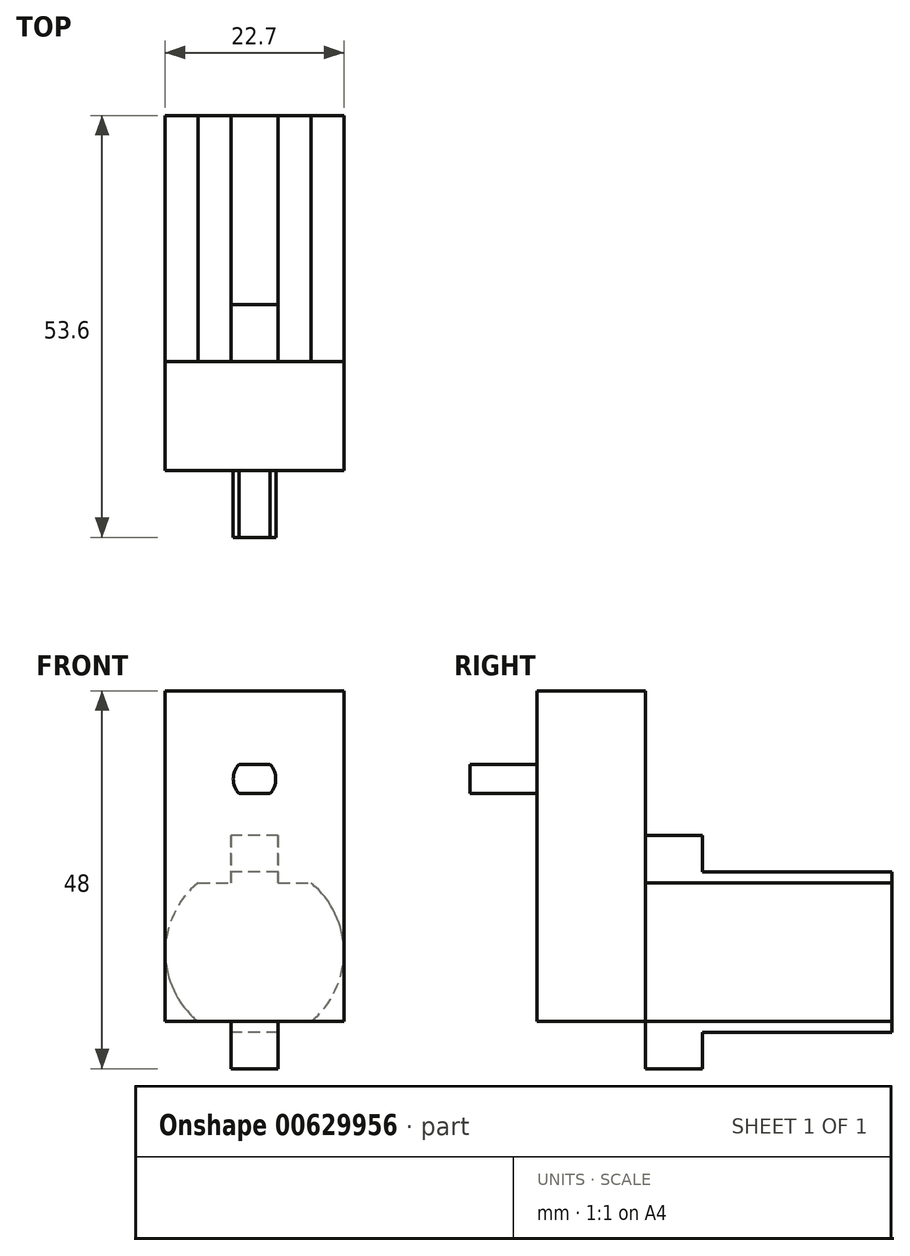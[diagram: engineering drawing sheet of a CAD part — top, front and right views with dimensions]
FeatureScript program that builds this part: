
annotation { "Feature Type Name" : "Feature", "Feature Type Description" : "" }
export const myFeature = defineFeature(function(context is Context, id is Id, definition is map)
    precondition{}
    {
        {
            var Q0;
            Q0=qCreatedBy(makeId("Front.planeOp"),FACE);
            var sketch = newSketch(context, id + "F0", { "sketchPlane" : qUnion([Q0])});
            skLineSegment(sketch, "E0.bottom", {"start": v(-11.35, 11.2) * mm, "end": v(11.35, 11.2) * mm});
            skLineSegment(sketch, "E0.top", {"start": v(-11.35, -30.8) * mm, "end": v(11.35, -30.8) * mm});
            skLineSegment(sketch, "E0.left", {"start": v(-11.35, 11.2) * mm, "end": v(-11.35, -30.8) * mm});
            skLineSegment(sketch, "E0.right", {"start": v(11.35, 11.2) * mm, "end": v(11.35, -30.8) * mm});
            skLineSegment(sketch, "E1", {"start": v(0, 11.2) * mm, "end": v(0, 0) * mm, "construction": true});
            skSolve(sketch);
        }
        {
            var Q0;
            Q0 = qSketchRegion(id + "F0", true);
            extrude(context, id + "F1", {"entities" : qUnion([Q0]), "oppositeDirection" : true, "depth" : 13.8 * mm, "offsetDistance" : 25.4 * mm});
        }
        {
            var Q0;
            Q0=makeQuery(id+"F1.opExtrude","CAP_FACE",FACE,{"disambiguationData":[OSD([sQuery(id+"F0.wireOp",EDGE,"E0.bottom"),sQuery(id+"F0.wireOp",EDGE,"E0.top"),sQuery(id+"F0.wireOp",EDGE,"E0.left"),sQuery(id+"F0.wireOp",EDGE,"E0.right")])],"isStart":true});
            var sketch = newSketch(context, id + "F2", { "sketchPlane" : qUnion([Q0])});
            skArc(sketch, "E2", {"start": v(-1.97, 1.85) * mm, "mid": v(-2.7, 0) * mm, "end": v(-1.97, -1.85) * mm});
            skLineSegment(sketch, "E3", {"start": v(-1.97, 1.85) * mm, "end": v(1.97, 1.85) * mm});
            skLineSegment(sketch, "E4", {"start": v(1.97, -1.85) * mm, "end": v(-1.97, -1.85) * mm});
            skArc(sketch, "E5.trimOffspring", {"start": v(1.97, -1.85) * mm, "mid": v(2.7, 0) * mm, "end": v(1.97, 1.85) * mm});
            skSolve(sketch);
        }
        {
            var Q0;
            Q0 = qSketchRegion(id + "F2", true);
            extrude(context, id + "F3", {"entities" : qUnion([Q0]), "operationType" : NewBodyOperationType.ADD, "depth" : 8.5 * mm, "offsetDistance" : 25.4 * mm});
        }
        {
            var Q0;
            Q0=makeQuery(id+"F1.opExtrude","CAP_FACE",FACE,{"disambiguationData":[OSD([sQuery(id+"F0.wireOp",EDGE,"E0.bottom"),sQuery(id+"F0.wireOp",EDGE,"E0.top"),sQuery(id+"F0.wireOp",EDGE,"E0.left"),sQuery(id+"F0.wireOp",EDGE,"E0.right")])],"isStart":true});
            var sketch = newSketch(context, id + "F4", { "sketchPlane" : qUnion([Q0])});
            skArc(sketch, "E6", {"start": v(-7.17, -13.2) * mm, "mid": v(-11.35, -22) * mm, "end": v(-7.17, -30.8) * mm});
            skLineSegment(sketch, "E7", {"start": v(-7.17, -30.8) * mm, "end": v(7.17, -30.8) * mm});
            skLineSegment(sketch, "E8", {"start": v(-7.17, -13.2) * mm, "end": v(7.17, -13.2) * mm});
            skArc(sketch, "E9.trimOffspring", {"start": v(7.17, -30.8) * mm, "mid": v(11.35, -22) * mm, "end": v(7.17, -13.2) * mm});
            skSolve(sketch);
        }
        {
            var Q0;
            Q0 = qSketchRegion(id + "F4", true);
            extrude(context, id + "F5", {"entities" : qUnion([Q0]), "operationType" : NewBodyOperationType.ADD, "oppositeDirection" : true, "depth" : 45.1 * mm, "offsetDistance" : 25.4 * mm});
        }
        {
            var Q0;
            Q0=qCreatedBy(makeId("Right.planeOp"),FACE);
            var sketch = newSketch(context, id + "F6", { "sketchPlane" : qUnion([Q0])});
            skLineSegment(sketch, "E10", {"start": v(13.8, -7.2) * mm, "end": v(21.07, -7.2) * mm});
            skLineSegment(sketch, "E11", {"start": v(21.07, -7.2) * mm, "end": v(21.07, -11.8) * mm});
            skLineSegment(sketch, "E12", {"start": v(21.07, -11.8) * mm, "end": v(45.1, -11.8) * mm});
            skLineSegment(sketch, "E13", {"start": v(45.1, -11.8) * mm, "end": v(45.1, -32.2) * mm});
            skLineSegment(sketch, "E14", {"start": v(45.1, -32.2) * mm, "end": v(21.07, -32.2) * mm});
            skLineSegment(sketch, "E15", {"start": v(21.07, -32.2) * mm, "end": v(21.07, -36.8) * mm});
            skLineSegment(sketch, "E16", {"start": v(21.07, -36.8) * mm, "end": v(13.8, -36.8) * mm});
            skLineSegment(sketch, "E17", {"start": v(13.8, -36.8) * mm, "end": v(13.8, -7.2) * mm});
            skLineSegment(sketch, "E18", {"start": v(45.1, -22) * mm, "end": v(0, -22) * mm, "construction": true});
            skSolve(sketch);
        }
        {
            var Q0;
            Q0 = qSketchRegion(id + "F6", true);
            extrude(context, id + "F7", {"entities" : qUnion([Q0]), "operationType" : NewBodyOperationType.ADD, "endBound" : BoundingType.SYMMETRIC, "depth" : 6 * mm, "offsetDistance" : 25.4 * mm});
        }
    });
